# Revit family: SHORT XS
name_source: partatom
category: Lighting Fixtures
units: mm (PartAtom-declared; Revit-internal decimal feet)

## family parameters
Cut with Voids When Loaded = No
Host = Face
Light Source = Yes
Maintain Annotation Orientation = Yes
Part Type = Normal
Room Calculation Point = No
Round Connector Dimension = Use Diameter
Shared = No

## types (3) — shared parameters
Color Filter = 16777215
Default Elevation = 1219 mm
Dimming Lamp Color Temperature Shift = <None>
Emit from Line Length = 610 mm
LuxLight_Alto = 103 mm  [stored 0.337927 ft]
LuxLight_AltoAreaLuminosa = 20 mm  [stored 0.0656168 ft]
LuxLight_Amperios = 350
LuxLight_Diametro = 80 mm  [stored 0.262467 ft]
LuxLight_DiametroAreaLuminosa = 58 mm  [stored 0.190289 ft]
LuxLight_Lumenes = 0 lm
LuxLight_Watios = 14 W
Manufacturer = LUXLIGHT
Tilt Angle = 0.00°
zero-valued in all types: LuxLight_Ancho, LuxLight_AnchoAreaLuminosa, LuxLight_Largo, LuxLight_LargoAreaLuminosa, LuxLight_ProtuberanciaTecho

## per-type parameters (varying)
| type | LuxLight_Temperatura | Photometric Web File |
| LXT036XS292 | 2700 K | LXT036XS292 .ies |
| LXT036XS293 | 3000 K | LXT036XS293 .ies |
| LXT036XS294 | 4000 K | LXT036XS294 .ies |

note: [stored X ft] marks values corroborated as IEEE doubles in the binary element streams (Revit-internal decimal feet)

## geometry (parser evidence)
native form markers: Sweep x2
no freeform markers — native parametric forms only
